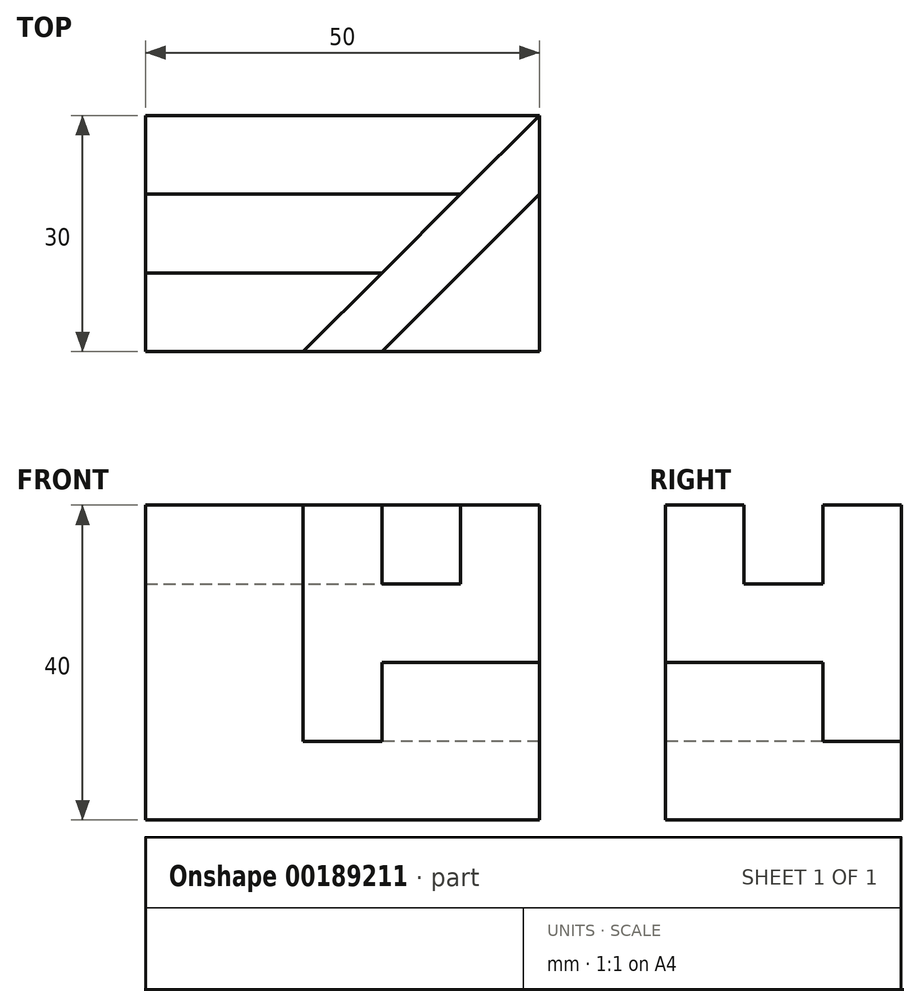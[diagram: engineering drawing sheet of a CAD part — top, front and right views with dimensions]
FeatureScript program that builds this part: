
annotation { "Feature Type Name" : "Feature", "Feature Type Description" : "" }
export const myFeature = defineFeature(function(context is Context, id is Id, definition is map)
    precondition{}
    {
        {
            var Q0;
            Q0=qCreatedBy(makeId("Top.planeOp"),FACE);
            var sketch = newSketch(context, id + "F0", { "sketchPlane" : qUnion([Q0])});
            skLineSegment(sketch, "E0.bottom", {"start": v(0, 0) * mm, "end": v(50, 0) * mm});
            skLineSegment(sketch, "E0.top", {"start": v(0, 30) * mm, "end": v(50, 30) * mm});
            skLineSegment(sketch, "E0.left", {"start": v(0, 0) * mm, "end": v(0, 30) * mm});
            skLineSegment(sketch, "E0.right", {"start": v(50, 0) * mm, "end": v(50, 30) * mm});
            skSolve(sketch);
        }
        {
            var Q0;
            Q0=makeQuery(id+"F0.imprint","IMPRINT",FACE,{"disambiguationData":[TD([[makeQuery(id+"F0.imprint","IMPRINT",EDGE,{"derivedFrom":sQuery(id+"F0.wireOp",EDGE,"E0.bottom")}),1.0]])]});
            extrude(context, id + "F1", {"entities" : qUnion([Q0]), "depth" : 40 * mm});
        }
        {
            var Q0;
            Q0=makeQuery(id+"F1.opExtrude","CAP_FACE",FACE,{"disambiguationData":[OSD([sQuery(id+"F0.wireOp",EDGE,"E0.bottom"),sQuery(id+"F0.wireOp",EDGE,"E0.top"),sQuery(id+"F0.wireOp",EDGE,"E0.left"),sQuery(id+"F0.wireOp",EDGE,"E0.right")])],"isStart":false});
            var sketch = newSketch(context, id + "F2", { "sketchPlane" : qUnion([Q0])});
            skLineSegment(sketch, "E1", {"start": v(50, 30) * mm, "end": v(20, 0) * mm});
            skLineSegment(sketch, "E2.0", {"start": v(20, 0) * mm, "end": v(50, 0) * mm});
            skLineSegment(sketch, "E3.0", {"start": v(50, 0) * mm, "end": v(50, 30) * mm});
            skPoint(sketch, "E4.orphan", {"position": v(0, 0) * mm});
            skSolve(sketch);
        }
        {
            var Q0;
            Q0=makeQuery(id+"F2.imprint","IMPRINT",FACE,{"disambiguationData":[TD([[makeQuery(id+"F2.imprint","IMPRINT",EDGE,{"derivedFrom":sQuery(id+"F2.wireOp",EDGE,"E1")}),1.0]])]});
            extrude(context, id + "F3", {"entities" : qUnion([Q0]), "operationType" : NewBodyOperationType.REMOVE, "oppositeDirection" : true, "depth" : 20 * mm});
        }
        {
            var Q0;
            Q0=makeQuery(id+"F3.boolean.opBoolean","COPY",FACE,{"derivedFrom":makeQuery(id+"F3.opExtrude","CAP_FACE",FACE,{"disambiguationData":[OSD([sQuery(id+"F2.wireOp",EDGE,"E1"),sQuery(id+"F2.wireOp",EDGE,"E2.0"),sQuery(id+"F2.wireOp",EDGE,"E3.0")])],"isStart":false})});
            var sketch = newSketch(context, id + "F4", { "sketchPlane" : qUnion([Q0])});
            skLineSegment(sketch, "E5.0", {"start": v(50, 30) * mm, "end": v(20, 0) * mm});
            skLineSegment(sketch, "E6.0", {"start": v(50, 20) * mm, "end": v(50, 30) * mm});
            skLineSegment(sketch, "E7.0", {"start": v(20, 0) * mm, "end": v(30, 0) * mm});
            skLineSegment(sketch, "E8", {"start": v(50, 20) * mm, "end": v(30, 0) * mm});
            skPoint(sketch, "E9.orphan", {"position": v(50, 0) * mm});
            skSolve(sketch);
        }
        {
            var Q0;
            Q0=makeQuery(id+"F4.imprint","IMPRINT",FACE,{"disambiguationData":[TD([[makeQuery(id+"F4.imprint","IMPRINT",EDGE,{"derivedFrom":sQuery(id+"F4.wireOp",EDGE,"E5.0")}),1.0]])]});
            extrude(context, id + "F5", {"entities" : qUnion([Q0]), "operationType" : NewBodyOperationType.REMOVE, "oppositeDirection" : true, "depth" : 10 * mm});
        }
        {
            var Q0;
            Q0=makeQuery(id+"F1.opExtrude","CAP_FACE",FACE,{"disambiguationData":[OSD([sQuery(id+"F0.wireOp",EDGE,"E0.bottom"),sQuery(id+"F0.wireOp",EDGE,"E0.top"),sQuery(id+"F0.wireOp",EDGE,"E0.left"),sQuery(id+"F0.wireOp",EDGE,"E0.right")])],"isStart":false});
            var sketch = newSketch(context, id + "F6", { "sketchPlane" : qUnion([Q0])});
            skLineSegment(sketch, "E10", {"start": v(0, 10) * mm, "end": v(30, 10) * mm});
            skLineSegment(sketch, "E11", {"start": v(0, 20) * mm, "end": v(40, 20) * mm});
            skLineSegment(sketch, "E12.0", {"start": v(0, 10) * mm, "end": v(0, 20) * mm});
            skLineSegment(sketch, "E13.0", {"start": v(40, 20) * mm, "end": v(30, 10) * mm});
            skPoint(sketch, "E14.orphan", {"position": v(20, 0) * mm});
            skPoint(sketch, "E15.orphan", {"position": v(50, 30) * mm});
            skPoint(sketch, "E16.orphan", {"position": v(0, 30) * mm});
            skPoint(sketch, "E17.orphan", {"position": v(0, 0) * mm});
            skSolve(sketch);
        }
        {
            var Q0;
            Q0=makeQuery(id+"F6.imprint","IMPRINT",FACE,{"disambiguationData":[TD([[makeQuery(id+"F6.imprint","IMPRINT",EDGE,{"derivedFrom":sQuery(id+"F6.wireOp",EDGE,"E10")}),1.0]])]});
            extrude(context, id + "F7", {"entities" : qUnion([Q0]), "operationType" : NewBodyOperationType.REMOVE, "oppositeDirection" : true, "depth" : 10 * mm});
        }
    });
